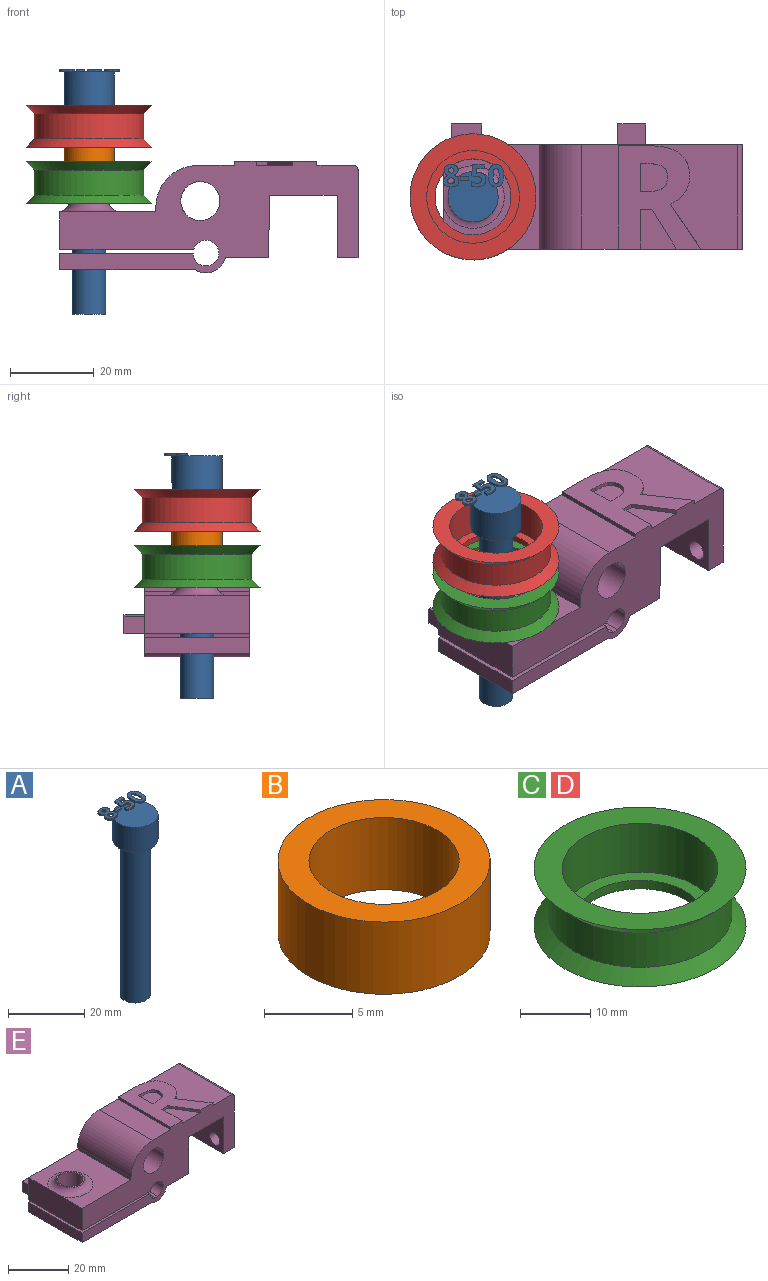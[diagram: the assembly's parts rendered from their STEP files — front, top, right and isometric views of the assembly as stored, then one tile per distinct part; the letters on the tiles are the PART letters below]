
ASSEMBLY  parts=5 mates=4
PART A: 86 faces, bbox 14.5x13.7x58.5 mm
  f0: plane 12x12mm, normal (0,0,1), area 99.4mm2, adj f5,f22,f23,f24,f25,f26,f40,f41
  f1: plane 1x0.26mm, normal (0,0,1), area 0.1mm2, adj f5,f46,f47,f48,f49
  f2: plane 0.85x0.68mm, normal (0,0,1), area 0.2mm2, adj f5,f29,f30,f31
  f3: cylinder r=4mm len=50mm, axis (0,0,-1), area 1256.6mm2, adj f4,f6
  f4: plane 8x8mm, normal (0,0,-1), area 50.3mm2, adj f3
  f5: cylinder r=6mm len=12mm, axis (0,0,-1), area 301.6mm2, adj f0,f1,f2,f6,f39,f45,f67,f85
  f6: plane 12x12mm, normal (0,0,-1), area 62.8mm2, adj f3,f5
  f7: extruded ~0.5x0.46mm, area 0.2mm2, adj f8,f37,f38,f39
  f8: extruded ~0.5x0.46mm, area 0.2mm2, adj f7,f9,f38,f39
  f9: extruded ~0.5x0.39mm, area 0.2mm2, adj f8,f10,f38,f39
  f10: extruded ~0.5x0.4mm, area 0.2mm2, adj f9,f11,f38,f39
  f11: extruded ~0.5x0.49mm, area 0.3mm2, adj f10,f12,f38,f39
  f12: extruded ~0.5x0.5mm, area 0.3mm2, adj f11,f13,f38,f39
  f13: extruded ~0.5x0.39mm, area 0.2mm2, adj f12,f37,f38,f39
  f14: extruded ~1.22x0.5mm, area 0.6mm2, adj f15,f35,f38,f39
  f15: extruded ~1.22x0.5mm, area 0.6mm2, adj f14,f16,f38,f39
  f16: extruded ~0.91x0.5mm, area 0.5mm2, adj f15,f17,f38,f39
  f17: extruded ~0.71x0.5mm, area 0.4mm2, adj f16,f18,f38,f39
  f18: extruded ~0.65x0.61mm, area 0.4mm2, adj f17,f19,f38,f39
  f19: extruded ~0.77x0.62mm, area 0.5mm2, adj f18,f20,f38,f39
  f20: extruded ~0.8x0.5mm, area 0.4mm2, adj f19,f21,f38,f39
  f21: extruded ~1.04x0.5mm, area 0.6mm2, adj f20,f22,f38,f39
  f22: extruded ~1.36x0.5mm, area 0.7mm2, adj f0,f21,f23,f38,f39
  f23: extruded ~1.33x0.5mm, area 0.7mm2, adj f0,f22,f24,f38
  f24: extruded ~1.04x0.51mm, area 0.6mm2, adj f0,f23,f25,f38
  f25: extruded ~0.75x0.5mm, area 0.4mm2, adj f0,f24,f26,f38
  f26: extruded ~0.85x0.66mm, area 0.5mm2, adj f0,f25,f27,f38,f39
  f27: extruded ~0.72x0.56mm, area 0.5mm2, adj f26,f28,f38,f39
  f28: extruded ~0.72x0.5mm, area 0.4mm2, adj f27,f35,f38,f39
  f29: extruded ~0.5x0.45mm, area 0.3mm2, adj f2,f30,f36,f38,f39
  f30: extruded ~0.5x0.47mm, area 0.3mm2, adj f2,f29,f31,f38
  f31: extruded ~0.62x0.5mm, area 0.3mm2, adj f2,f30,f32,f38,f39
  f32: extruded ~0.59x0.5mm, area 0.3mm2, adj f31,f33,f38,f39
  f33: extruded ~0.5x0.48mm, area 0.3mm2, adj f32,f34,f38,f39
  f34: extruded ~0.89x0.77mm, area 0.6mm2, adj f33,f36,f38,f39
  f35: extruded ~0.93x0.5mm, area 0.5mm2, adj f14,f28,f38,f39
  f36: extruded ~0.66x0.5mm, area 0.4mm2, adj f29,f34,f38,f39
  f37: extruded ~0.5x0.39mm, area 0.2mm2, adj f7,f13,f38,f39
  f38: plane 5.4x3.69mm, normal (0,0,1), area 12.7mm2, adj f7,f8,f9,f10,f11,f12,f13,f14
  f39: plane 5.4x3.53mm, normal (0,0,-1), area 10.2mm2, adj f5,f7,f8,f9,f10,f11,f12,f13
  f40: plane 0.9x0.5mm, normal (-1,0,0), area 0.4mm2, adj f0,f41,f43,f44
  f41: plane 1.93x0.5mm, normal (0,-1,0), area 1mm2, adj f0,f40,f42,f44
  f42: plane 0.9x0.5mm, normal (1,0,0), area 0.4mm2, adj f0,f41,f43,f44
  f43: plane 1.93x0.5mm, normal (0,1,0), area 1mm2, adj f0,f40,f42,f44
  f44: plane 1.93x0.9mm, normal (0,0,1), area 1.7mm2, adj f40,f41,f42,f43
  f45: plane 0.76x0.31mm, normal (0,0,-1), area 0mm2, adj f5,f46
  f46: extruded ~1.21x0.5mm, area 0.7mm2, adj f0,f1,f45,f47,f65,f66
  f47: extruded ~0.54x0.5mm, area 0.3mm2, adj f1,f46,f48,f66
  f48: plane 0.5x0.13mm, normal (-0.2,0.98,0), area 0.1mm2, adj f1,f47,f49,f66
  f49: plane 1.03x0.5mm, normal (1,-0.09,0), area 0.5mm2, adj f1,f48,f50,f66,f67
  f50: plane 1.88x0.5mm, normal (0,-1,0), area 0.9mm2, adj f49,f51,f66,f67
  f51: plane 0.94x0.5mm, normal (1,0,0), area 0.5mm2, adj f50,f52,f66,f67
  f52: plane 2.85x0.5mm, normal (0,1,0), area 1.4mm2, adj f51,f53,f66,f67
  f53: plane 2.68x0.5mm, normal (-1,0.07,0), area 1.3mm2, adj f0,f52,f54,f66,f67
  f54: plane 0.5x0.44mm, normal (-0.47,-0.88,0), area 0.3mm2, adj f0,f53,f55,f66
  f55: extruded ~0.5x0.37mm, area 0.2mm2, adj f0,f54,f56,f66
  f56: extruded ~0.5x0.42mm, area 0.2mm2, adj f0,f55,f57,f66
  f57: extruded ~1.05x0.8mm, area 0.8mm2, adj f0,f56,f58,f66
  f58: extruded ~1.02x0.83mm, area 0.8mm2, adj f0,f57,f59,f66
  f59: extruded ~0.72x0.5mm, area 0.4mm2, adj f0,f58,f60,f66
  f60: extruded ~0.66x0.5mm, area 0.4mm2, adj f0,f59,f61,f66
  f61: plane 0.96x0.5mm, normal (-1,0,0), area 0.5mm2, adj f0,f60,f62,f66
  f62: extruded ~1.42x0.5mm, area 0.7mm2, adj f0,f61,f63,f66
  f63: extruded ~1.55x0.5mm, area 0.8mm2, adj f0,f62,f64,f66
  f64: extruded ~1.36x0.54mm, area 0.8mm2, adj f0,f63,f65,f66
  f65: extruded ~1.17x0.5mm, area 0.6mm2, adj f0,f46,f64,f66
  f66: plane 5.33x3.51mm, normal (0,0,1), area 10.9mm2, adj f46,f47,f48,f49,f50,f51,f52,f53
  f67: plane 2.97x1.71mm, normal (0,0,-1), area 3.5mm2, adj f5,f49,f50,f51,f52,f53
  f68: extruded ~1.39x0.5mm, area 0.7mm2, adj f69,f83,f84,f85
  f69: extruded ~1.39x0.5mm, area 0.7mm2, adj f68,f70,f84,f85
  f70: extruded ~0.56x0.5mm, area 0.4mm2, adj f69,f71,f84,f85
  f71: extruded ~0.56x0.5mm, area 0.4mm2, adj f70,f72,f84,f85
  f72: extruded ~1.39x0.5mm, area 0.7mm2, adj f71,f73,f84,f85
  f73: extruded ~1.38x0.5mm, area 0.7mm2, adj f72,f74,f84,f85
  f74: extruded ~0.56x0.5mm, area 0.4mm2, adj f73,f83,f84,f85
  f75: extruded ~2.04x0.5mm, area 1.1mm2, adj f76,f82,f84,f85
  f76: extruded ~2.02x0.5mm, area 1.1mm2, adj f75,f77,f84,f85
  f77: extruded ~1.38x0.69mm, area 0.8mm2, adj f76,f78,f84,f85
  f78: extruded ~1.38x0.66mm, area 0.8mm2, adj f77,f79,f84,f85
  f79: extruded ~2.05x0.5mm, area 1.1mm2, adj f78,f80,f84,f85
  f80: extruded ~2.02x0.5mm, area 1mm2, adj f0,f79,f81,f84,f85
  f81: extruded ~1.37x0.68mm, area 0.8mm2, adj f0,f80,f82,f84
  f82: extruded ~1.39x0.66mm, area 0.8mm2, adj f0,f75,f81,f84,f85
  f83: extruded ~0.56x0.5mm, area 0.4mm2, adj f68,f74,f84,f85
  f84: plane 5.41x3.68mm, normal (0,0,1), area 12.1mm2, adj f68,f69,f70,f71,f72,f73,f74,f75
  f85: plane 5.41x3.68mm, normal (0,0,-1), area 10.3mm2, adj f5,f68,f69,f70,f71,f72,f73,f74
PART B: 4 faces, bbox 12x12x5 mm
  f0: cylinder r=4.25mm len=8.5mm, axis (0,0,-1), area 133.5mm2, adj f2,f3
  f1: cylinder r=6mm len=12mm, axis (0,0,-1), area 188.5mm2, adj f2,f3
  f2: plane 12x12mm, normal (0,0,1), area 56.4mm2, adj f0,f1
  f3: plane 12x12mm, normal (0,0,-1), area 56.4mm2, adj f0,f1
PART C: 8 faces, bbox 30.2x30.2x10 mm
  f0: plane 30.2x30.2mm, normal (0,0,1), area 329.2mm2, adj f1,f7
  f1: cylinder r=11.1mm len=22.2mm, axis (0,0,-1), area 592.8mm2, adj f0,f2
  f2: plane 22.2x22.2mm, normal (0,0,1), area 126.9mm2, adj f1,f3
  f3: cylinder r=9.1mm len=18.2mm, axis (0,0,-1), area 85.8mm2, adj f2,f4
  f4: plane 30.2x30.2mm, normal (0,0,-1), area 456.2mm2, adj f3,f5
  f5: cone r=13.1mm half-angle=45deg, axis (0,0,-1), area 250.6mm2, adj f4,f6
  f6: cylinder r=13.1mm len=26.2mm, axis (0,0,-1), area 493.9mm2, adj f5,f7
  f7: cone r=15.1mm half-angle=45deg, axis (0,0,1), area 250.6mm2, adj f0,f6
PART D: same geometry as C
PART E: 58 faces, bbox 74.9x30x26.7 mm
  f0: cylinder r=4.75mm len=25mm, axis (0,-1,0), area 229mm2, adj f6,f7,f16,f17
  f1: cylinder r=3.1mm len=25mm, axis (0,-1,0), area 100.9mm2, adj f16,f17,f20,f57
  f2: plane 37.42x25mm, normal (0,0,1), area 542.1mm2, adj f16,f17,f26,f28,f41,f42,f43,f44
  f3: plane 9.51x8.71mm, normal (0,0,1), area 54.7mm2, adj f16,f38,f39,f40
  f4: plane 25x3.85mm, normal (-1,0,0), area 96.2mm2, adj f7,f16,f17,f20
  f5: cylinder r=4.17mm len=8.35mm, axis (0,0,1), area 100.9mm2, adj f7,f20
  f6: plane 25x10.36mm, normal (0,0,-1), area 258.9mm2, adj f0,f15,f16,f17
  f7: plane 32.45x25mm, normal (0,0,-1), area 756.5mm2, adj f0,f4,f5,f16,f17
  f8: plane 25x9.1mm, normal (-1,0,0), area 226.5mm2, adj f9,f16,f17,f21,f25
  f9: plane 25x23mm, normal (0,0,1), area 400mm2, adj f8,f10,f16,f17,f25
  f10: plane 25x1.1mm, normal (-1,0,0), area 27.5mm2, adj f9,f16,f17,f26
  f11: plane 25x21.09mm, normal (1,0,0), area 493.5mm2, adj f12,f16,f17,f23,f24,f28
  f12: plane 25x5mm, normal (0,0,-1), area 125mm2, adj f11,f13,f16,f17
  f13: plane 25x15mm, normal (-1,0,0), area 341.3mm2, adj f12,f14,f16,f17,f23,f24
  f14: plane 25x16.2mm, normal (0,0,-1), area 405mm2, adj f13,f15,f16,f17
  f15: plane 25x14.91mm, normal (1,0,-0.01), area 372.8mm2, adj f6,f14,f16,f17
  f16: plane 71.42x26.75mm, normal (0,-1,0), area 1051.2mm2, adj f0,f1,f2,f3,f4,f6,f7,f8
  f17: plane 71.42x25.75mm, normal (0,1,0), area 980.1mm2, adj f0,f1,f2,f4,f6,f7,f8,f9
  f18: cylinder r=4.17mm len=11.05mm, axis (0,0,1), area 290mm2, adj f21,f22
  f19: cylinder r=3.1mm len=25mm, axis (0,-1,0), area 326.8mm2, adj f16,f17,f21,f57
  f20: plane 31.91x25mm, normal (0,0,1), area 743.1mm2, adj f1,f4,f5,f16,f17
  f21: plane 32.03x30mm, normal (0,0,-1), area 782.4mm2, adj f8,f16,f17,f18,f19,f30,f31,f32
  f22: plane 9.35x9.35mm, normal (0,0,1), area 13.9mm2, adj f18,f25
  f23: cylinder r=2.43mm len=5mm, axis (1,0,0), area 76.2mm2, adj f11,f13
  f24: cylinder r=2.2mm len=5mm, axis (1,0,0), area 69.1mm2, adj f11,f13
  f25: torus R=7.5mm, axis (0,0,-1), area 134.6mm2, adj f8,f9,f22
  f26: cylinder r=10mm len=25mm, axis (0,-1,0), area 392.7mm2, adj f2,f10,f16,f17
  f27: cylinder r=4.68mm len=25mm, axis (0,-1,0), area 735.2mm2, adj f16,f17
  f28: cylinder r=1mm len=25mm, axis (0,-1,0), area 39.3mm2, adj f2,f11,f16,f17
  f29: plane 7.3x5mm, normal (0,0,1), area 36.5mm2, adj f17,f30,f31,f32
  f30: plane 5x4.12mm, normal (-1,0,0), area 20.6mm2, adj f17,f21,f29,f32
  f31: plane 5x4.12mm, normal (1,0,0), area 20.6mm2, adj f17,f21,f29,f32
  f32: plane 7.3x4.12mm, normal (0,1,0), area 30.1mm2, adj f21,f29,f30,f31
  f33: plane 6.63x5mm, normal (0,0,1), area 33.2mm2, adj f17,f34,f36,f37
  f34: plane 5x4.5mm, normal (-1,0,0), area 22.5mm2, adj f17,f33,f35,f37
  f35: plane 6.63x5mm, normal (0,0,-1), area 33.2mm2, adj f17,f34,f36,f37
  f36: plane 5x4.5mm, normal (1,0,0), area 22.5mm2, adj f17,f33,f35,f37
  f37: plane 6.63x4.5mm, normal (0,1,0), area 29.9mm2, adj f33,f34,f35,f36
  f38: plane 9.51x1mm, normal (1,0,0), area 9.5mm2, adj f3,f16,f39,f55
  f39: plane 2.79x1mm, normal (0,-1,0), area 2.8mm2, adj f3,f38,f40,f55
  f40: plane 9.51x5.92mm, normal (-0.85,-0.53,0), area 11.2mm2, adj f3,f16,f39,f55
  f41: extruded ~10.8x7.29mm, area 13mm2, adj f2,f16,f42,f55
  f42: extruded ~3.41x2.67mm, area 4.4mm2, adj f2,f41,f43,f55
  f43: extruded ~3.89x1.2mm, area 4.1mm2, adj f2,f42,f44,f55
  f44: extruded ~5.59x2.42mm, area 6.3mm2, adj f2,f43,f45,f55
  f45: extruded ~7.48x1.84mm, area 7.8mm2, adj f2,f44,f46,f55
  f46: plane 7.22x1mm, normal (0,1,0), area 7.2mm2, adj f2,f45,f47,f55
  f47: plane 24.79x1mm, normal (-1,0,0), area 24.8mm2, adj f2,f16,f46,f55
  f48: plane 1.69x1mm, normal (0,1,0), area 1.7mm2, adj f49,f54,f55,f56
  f49: plane 6.7x1mm, normal (1,0,0), area 6.7mm2, adj f48,f50,f55,f56
  f50: plane 1.6x1mm, normal (0,-1,0), area 1.6mm2, adj f49,f51,f55,f56
  f51: extruded ~3.75x1mm, area 3.9mm2, adj f50,f52,f55,f56
  f52: extruded ~2.51x1.21mm, area 2.9mm2, adj f51,f53,f55,f56
  f53: extruded ~2.61x1.19mm, area 3mm2, adj f52,f54,f55,f56
  f54: extruded ~3.68x1mm, area 3.8mm2, adj f48,f53,f55,f56
  f55: plane 24.79x19.8mm, normal (0,0,1), area 300mm2, adj f16,f38,f39,f40,f41,f42,f43,f44
  f56: plane 6.7x6.56mm, normal (0,0,1), area 38.8mm2, adj f48,f49,f50,f51,f52,f53,f54
  f57: plane 25x1.35mm, normal (0,0,1), area 33.7mm2, adj f1,f16,f17,f19
PLACE A t=(-103.78,-12.5,-13.6)mm
PLACE B rot(axis=(1,0,0),180deg) t=(-103.78,-12.5,26.4)mm
PLACE C t=(-103.78,-12.5,18.1)mm
PLACE D t=(-103.78,-12.5,31.6)mm
PLACE E at identity
MATE fastened A.f3 <-> D.f1  axis (0,0,-1) through (-103.78,-12.5,36.4)mm
MATE fastened B.f0 <-> C.f1  axis (0,0,1) through (-103.78,-12.5,21.4)mm
MATE fastened C.f1 <-> E.f5  axis (0,0,-1) through (-103.78,-12.5,12.9)mm
MATE fastened D.f1 <-> B.f0  axis (0,0,-1) through (-103.78,-12.5,26.4)mm
